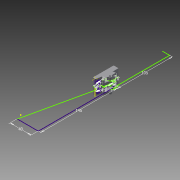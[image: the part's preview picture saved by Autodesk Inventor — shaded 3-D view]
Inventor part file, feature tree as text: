
AUTODESK INVENTOR PART (.ipt)
format: ipt  version: 2015 (Build 190159000, 159)  size: 179,712 bytes
history: native  units: in
note: dims shown in document units (in); Inventor stores cm internally (conversion verified against a paired STEP export)
features: extrude x7, sketch x2
ambient origin geometry x8: Origin, YZ Plane, XZ Plane, XY Plane, X Axis, Y Axis, Z Axis, Center Point
bodies: Body1 (feature_tree)
feature tree (9):
  extrude  "Extrusion4"  Depth=0.1181in
  extrude  "Extrusion5"  Depth=0.1181in
  extrude  "Extrusion6"  Depth=0.3937in
  extrude  "Extrusion7"  Depth=0.3937in
  sketch  "Sketch2"  dims[d0=5.7087in d1=0.1181in]
  extrude  "Extrusion8"  Depth=0.3937in
  extrude  "Extrusion9"  Depth=0.3937in
  extrude  "Extrusion10"  Depth=0.3937in
  sketch  "Sketch3"  dims[d2=0.1969in d4=0.1181in d5=1.5748in d6=4.1339in d7=0.8661in d8=0.2362in d10=0.3937in d11=0.3937in d12=0.1969in d13=0.1969in d20=0.6693in d21=1.1024in d22=0.0in d23=0.7283in d24=0.0in d25=0.4134in d26=0.0in d27=0.374in d28=0.0in d29=0.1969in d30=0.2756in d31=0.2756in d32=0.189in d33=0.189in d34=0.315in d35=0.315in d36=0.4134in d37=0.0in d38=0.1969in d39=0.0in d40=0.1969in d41=0.2756in d42=0.2756in d43=0.189in d44=0.189in d45=0.3937in d46=0.0in]
